# Revit family: Flushometer-Urinal_Touchless-KOHLER-Tripoint-K-7537
name_source: partatom
category: Plumbing Fixtures
revit_build: Autodesk Revit 2015 (Build: 20140606_1530(x64)
units: mm (PartAtom-declared; Revit-internal decimal feet)

## types (2) — shared parameters
ADA Compliant = Yes
Assembly Code = D2020
CW Connection = Yes
Cold Water Inlet = Cold Water Inlet
Cold Water Outlet = Cold Water Outlet
Date Modified = 2/13/2019
Default Elevation = 0"
Finish = Kohler-Metal-CP-Polished_Chrome
Flow Rate = 10 GPM
Flush Rate = 0.5 GPF
HW Connection = No
Hot Water Inlet = Hot Water Inlet
Manufacturer = KOHLER Co.
MasterFormat 1995 = 154300
MasterFormat 2004 = 22.11.00
Material = Brass Construction
Pressure = 80.00 psi
Product Documentation Link = https://www.us.kohler.com
Product Name = Tripoint
Product Page URL = http://www.us.kohler.com
URL = https://www.us.kohler.com
Vent Connection = No
Waste Connection = No
Waste Water Outlet = Waste Water Outlet
WaterSense Certified = No

## per-type parameters (varying)
| type | Description | Model | Type |
| 0.5 GPF Flushometer,CP-Polished Chrome | Exposed hybrid 0.5 gpf flushometer for urinal installation | K-7537-CP | 1 |
| 0.5 GPF Retrofit Flushometer,CP-Polished Chrome | Exposed hybrid 0.5 gpf retrofit flushometer for urinal installation | K-7537-RF-CP | 2 |

## geometry (parser evidence)
native form markers: Sweep x7
no freeform markers — native parametric forms only
